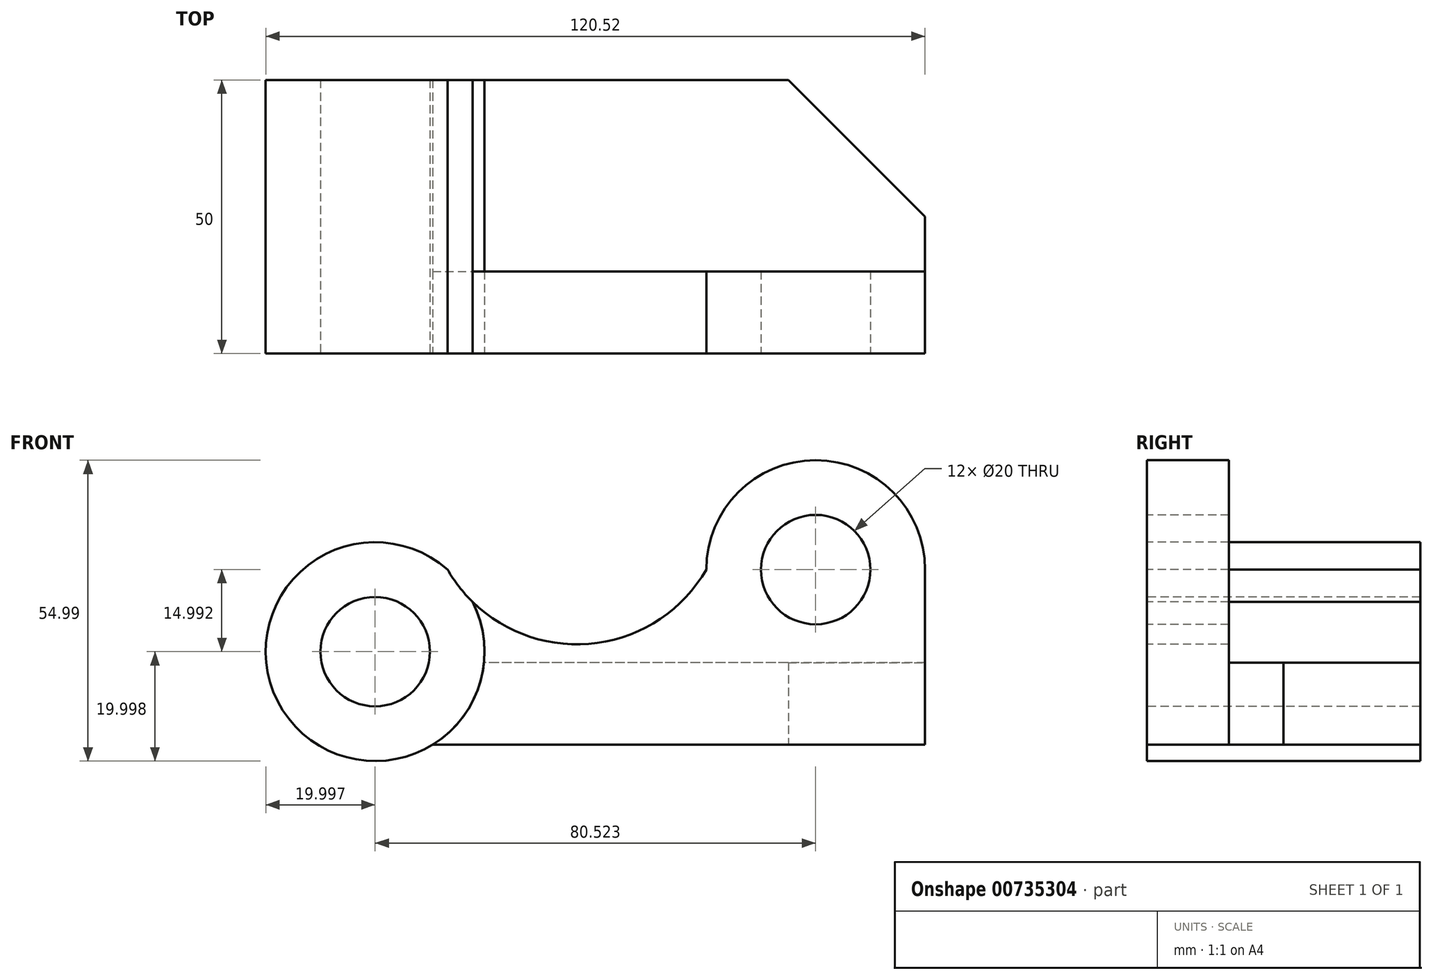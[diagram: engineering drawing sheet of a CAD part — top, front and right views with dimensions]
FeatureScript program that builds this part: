
annotation { "Feature Type Name" : "Feature", "Feature Type Description" : "" }
export const myFeature = defineFeature(function(context is Context, id is Id, definition is map)
    precondition{}
    {
        {
            var Q0;
            Q0=qCreatedBy(makeId("Front.planeOp"),FACE);
            var sketch = newSketch(context, id + "F0", { "sketchPlane" : qUnion([Q0])});
            skLineSegment(sketch, "E0", {"start": v(40, 0) * mm, "end": v(40, 32) * mm});
            skArc(sketch, "E1", {"start": v(40, 32) * mm, "mid": v(20, 52) * mm, "end": v(0, 32) * mm});
            skArc(sketch, "E2", {"start": v(-47.29, 32) * mm, "mid": v(-23.64, 18.34) * mm, "end": v(0, 32) * mm});
            skLineSegment(sketch, "E3", {"start": v(-50, 0) * mm, "end": v(40, 0) * mm});
            skArc(sketch, "E4", {"start": v(-50, 0) * mm, "mid": v(-40.6, 15.32) * mm, "end": v(-47.29, 32) * mm});
            skCircle(sketch, "E5", {"center": v(-60.52, 17) * mm, "radius": 20 * mm});
            skCircle(sketch, "E6", {"center": v(-60.52, 17) * mm, "radius": 10 * mm});
            skCircle(sketch, "E7", {"center": v(20, 32) * mm, "radius": 10 * mm});
            skSolve(sketch);
        }
        {
            var Q0;
            Q0=makeQuery(id+"F0.imprint","IMPRINT",FACE,{"disambiguationData":[TD([[makeQuery(id+"F0.imprint","IMPRINT",EDGE,{"derivedFrom":sQuery(id+"F0.wireOp",EDGE,"E0")}),1.0]])]});
            extrude(context, id + "F1", {"entities" : qUnion([Q0]), "oppositeDirection" : true, "depth" : 15 * mm, "offsetDistance" : 25 * mm});
        }
        {
            var Q0;
            {var subQ0=sQuery(id+"F0.wireOp",EDGE,"E5");var subQ1=sQuery(id+"F0.wireOp",EDGE,"E2");var subQ2=makeQuery(id+"F0.imprint","INTERSECT",VERTEX,{"disambiguationData":[OD(0.0)],"derivedFrom":[subQ1,subQ0]});Q0=makeQuery(id+"F0.imprint","IMPRINT",FACE,{"disambiguationData":[TD([[makeQuery(id+"F0.imprint","IMPRINT",EDGE,{"disambiguationData":[TD([[subQ2,-1.0]])],"derivedFrom":subQ1}),-1.0]])]});}
            extrude(context, id + "F2", {"entities" : qUnion([Q0]), "oppositeDirection" : true, "depth" : 50 * mm, "offsetDistance" : 25 * mm});
        }
        {
            var Q0;
            Q0=makeQuery(id+"F0.imprint","IMPRINT",FACE,{"disambiguationData":[TD([[makeQuery(id+"F0.imprint","IMPRINT",EDGE,{"derivedFrom":sQuery(id+"F0.wireOp",EDGE,"E6")}),1.0]])]});
            extrude(context, id + "F3", {"entities" : qUnion([Q0]), "operationType" : NewBodyOperationType.REMOVE, "oppositeDirection" : true, "depth" : 50 * mm, "offsetDistance" : 25 * mm});
        }
        {
            var Q0;
            Q0=makeQuery(id+"F1.opExtrude","CAP_FACE",FACE,{"disambiguationData":[OSD([sQuery(id+"F0.wireOp",EDGE,"E0"),sQuery(id+"F0.wireOp",EDGE,"E1"),sQuery(id+"F0.wireOp",EDGE,"E2"),sQuery(id+"F0.wireOp",EDGE,"E3"),sQuery(id+"F0.wireOp",EDGE,"E5"),sQuery(id+"F0.wireOp",EDGE,"E7")])],"isStart":false});
            var sketch = newSketch(context, id + "F4", { "sketchPlane" : qUnion([Q0])});
            skLineSegment(sketch, "E8", {"start": v(-40, 15) * mm, "end": v(40.62, 15) * mm});
            skCircle(sketch, "E9", {"center": v(60.52, 17) * mm, "radius": 20 * mm});
            skPoint(sketch, "E9.second.point", {"position": v(50, 0) * mm});
            skPoint(sketch, "E9.third.point", {"position": v(46.9, 2.37) * mm});
            skLineSegment(sketch, "E10", {"start": v(-40, 15) * mm, "end": v(-40, 0) * mm});
            skLineSegment(sketch, "E11", {"start": v(-40, 0) * mm, "end": v(50, 0) * mm});
            skSolve(sketch);
        }
        {
            var Q0;
            {var subQ0=sQuery(id+"F4.wireOp",EDGE,"E8");Q0=makeQuery(id+"F4.imprint","IMPRINT",FACE,{"disambiguationData":[TD([[makeQuery(id+"F4.imprint","IMPRINT",EDGE,{"derivedFrom":subQ0}),-1.0]])]});}
            extrude(context, id + "F5", {"entities" : qUnion([Q0]), "depth" : 35 * mm, "offsetDistance" : 25 * mm});
        }
        {
            var Q0;
            Q0=makeQuery(id+"F5.opExtrude","CAP_EDGE",EDGE,{"disambiguationData":[OSD([sQuery(id+"F4.wireOp",EDGE,"E10")])],"isStart":false});
            chamfer(context, id + "F6", {"entities" : qUnion([Q0]), "width" : 25 * mm, "tangentPropagation" : true});
        }
    });
